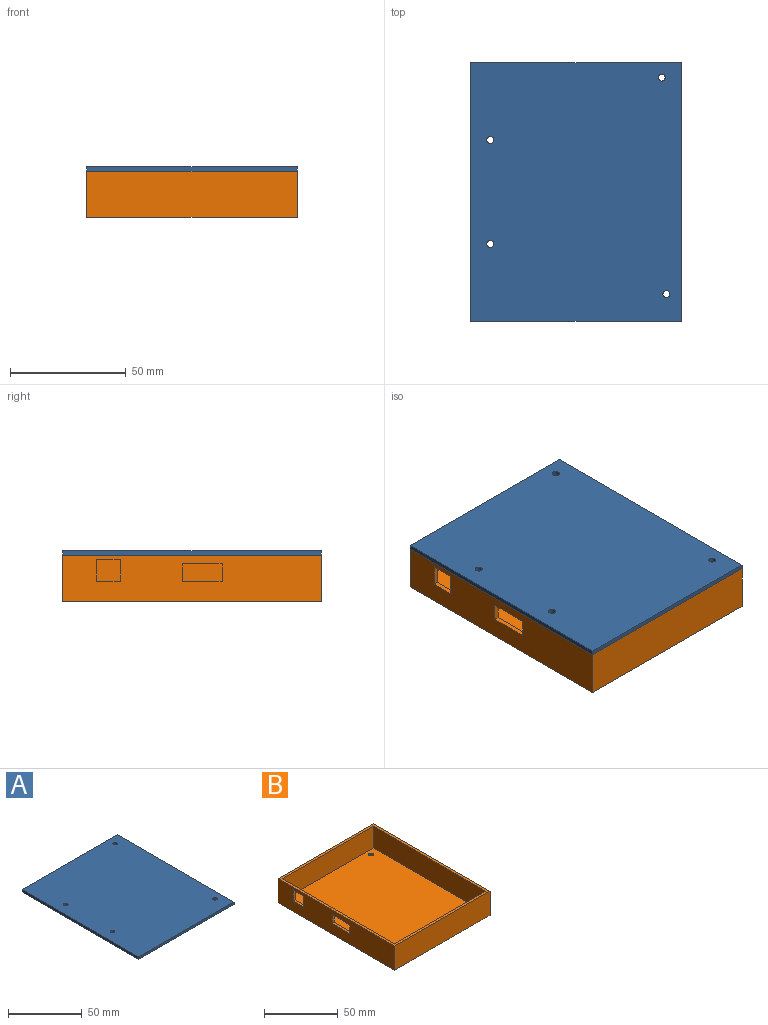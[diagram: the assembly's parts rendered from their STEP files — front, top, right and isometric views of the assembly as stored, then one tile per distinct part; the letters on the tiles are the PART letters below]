
ASSEMBLY  parts=2 mates=1
PART A: 20 faces, bbox 91.3x112x4 mm
  f0: plane 112x2mm, normal (1,0,0), area 224mm2, adj f1,f3,f4,f5
  f1: plane 91.25x2mm, normal (0,1,0), area 182.5mm2, adj f0,f2,f4,f5
  f2: plane 112x2mm, normal (-1,0,0), area 224mm2, adj f1,f3,f4,f5
  f3: plane 91.25x2mm, normal (0,-1,0), area 182.5mm2, adj f0,f2,f4,f5
  f4: plane 112x91.25mm, normal (0,0,1), area 10191.7mm2, adj f0,f1,f2,f3,f16,f17,f18,f19
  f5: plane 112x91.25mm, normal (0,0,-1), area 797mm2, adj f0,f1,f2,f3,f12,f13,f14,f15
  f6: plane 106x85.25mm, normal (0,0,-1), area 9008.2mm2, adj f8,f9,f10,f11,f16,f17,f18,f19
  f7: plane 108x87.25mm, normal (0,0,-1), area 386.5mm2, adj f8,f9,f10,f11,f12,f13,f14,f15
  f8: plane 85.25x2mm, normal (0,1,0), area 170.5mm2, adj f6,f7,f9,f11
  f9: plane 106x2mm, normal (1,0,0), area 212mm2, adj f6,f7,f8,f10
  f10: plane 85.25x2mm, normal (0,-1,0), area 170.5mm2, adj f6,f7,f9,f11
  f11: plane 106x2mm, normal (-1,0,0), area 212mm2, adj f6,f7,f8,f10
  f12: plane 108x2mm, normal (-1,0,0), area 216mm2, adj f5,f7,f13,f15
  f13: plane 87.25x2mm, normal (0,1,0), area 174.5mm2, adj f5,f7,f12,f14
  f14: plane 108x2mm, normal (1,0,0), area 216mm2, adj f5,f7,f13,f15
  f15: plane 87.25x2mm, normal (0,-1,0), area 174.5mm2, adj f5,f7,f12,f14
  f16: cylinder r=1.5mm len=3mm, axis (0,0,1), area 18.8mm2, adj f4,f6
  f17: cylinder r=1.5mm len=3mm, axis (0,0,1), area 18.8mm2, adj f4,f6
  f18: cylinder r=1.5mm len=3mm, axis (0,0,1), area 18.8mm2, adj f4,f6
  f19: cylinder r=1.5mm len=3mm, axis (0,0,1), area 18.8mm2, adj f4,f6
PART B: 31 faces, bbox 91.3x112x20 mm
  f0: plane 108x18mm, normal (1,0,0), area 1723.6mm2, adj f2,f4,f6,f10,f11,f12,f13,f14
  f1: plane 112x20mm, normal (-1,0,0), area 2019.6mm2, adj f3,f7,f9,f10,f11,f12,f13,f14
  f2: plane 108x87.25mm, normal (0,0,1), area 9386.7mm2, adj f0,f4,f5,f6,f19,f22,f25,f28
  f3: plane 112x91.25mm, normal (0,0,-1), area 10153.5mm2, adj f1,f7,f8,f9,f21,f24,f27,f30
  f4: plane 87.25x18mm, normal (0,1,0), area 1570.5mm2, adj f0,f2,f5,f10
  f5: plane 108x18mm, normal (-1,0,0), area 1944mm2, adj f2,f4,f6,f10
  f6: plane 87.25x18mm, normal (0,-1,0), area 1570.5mm2, adj f0,f2,f5,f10
  f7: plane 91.25x20mm, normal (0,-1,0), area 1825mm2, adj f1,f3,f8,f10
  f8: plane 112x20mm, normal (1,0,0), area 2240mm2, adj f3,f7,f9,f10
  f9: plane 91.25x20mm, normal (0,1,0), area 1825mm2, adj f1,f3,f8,f10
  f10: plane 112x91.25mm, normal (0,0,1), area 797mm2, adj f0,f1,f4,f5,f6,f7,f8,f9
  f11: plane 7.4x2mm, normal (0,-1,0), area 14.8mm2, adj f0,f1,f12,f14
  f12: plane 17.1x2mm, normal (0,0,1), area 34.2mm2, adj f0,f1,f11,f13
  f13: plane 7.4x2mm, normal (0,1,0), area 14.8mm2, adj f0,f1,f12,f14
  f14: plane 17.1x2mm, normal (0,0,-1), area 34.2mm2, adj f0,f1,f11,f13
  f15: plane 9.2x2mm, normal (0,-1,0), area 18.4mm2, adj f0,f1,f16,f18
  f16: plane 10.2x2mm, normal (0,0,1), area 20.4mm2, adj f0,f1,f15,f17
  f17: plane 9.2x2mm, normal (0,1,0), area 18.4mm2, adj f0,f1,f16,f18
  f18: plane 10.2x2mm, normal (0,0,-1), area 20.4mm2, adj f0,f1,f15,f17
  f19: cylinder r=1.7mm len=3.4mm, axis (0,0,-1), area 10.7mm2, adj f2,f20
  f20: plane 4.6x4.6mm, normal (0,0,-1), area 7.5mm2, adj f19,f21
  f21: cylinder r=2.3mm len=4.6mm, axis (0,0,-1), area 14.5mm2, adj f3,f20
  f22: cylinder r=1.7mm len=3.4mm, axis (0,0,-1), area 10.7mm2, adj f2,f23
  f23: plane 4.6x4.6mm, normal (0,0,-1), area 7.5mm2, adj f22,f24
  f24: cylinder r=2.3mm len=4.6mm, axis (0,0,-1), area 14.5mm2, adj f3,f23
  f25: cylinder r=1.7mm len=3.4mm, axis (0,0,-1), area 10.7mm2, adj f2,f26
  f26: plane 4.6x4.6mm, normal (0,0,-1), area 7.5mm2, adj f25,f27
  f27: cylinder r=2.3mm len=4.6mm, axis (0,0,-1), area 14.5mm2, adj f3,f26
  f28: cylinder r=1.7mm len=3.4mm, axis (0,0,-1), area 10.7mm2, adj f2,f29
  f29: plane 4.6x4.6mm, normal (0,0,-1), area 7.5mm2, adj f28,f30
  f30: cylinder r=2.3mm len=4.6mm, axis (0,0,-1), area 14.5mm2, adj f3,f29
PLACE A t=(5.71,-65.33,50.37)mm
PLACE B t=(5.71,-65.33,30.37)mm
MATE fastened B.f10 <-> A.f5  axis (0,0,1) through (7.71,-67.33,50.37)mm
